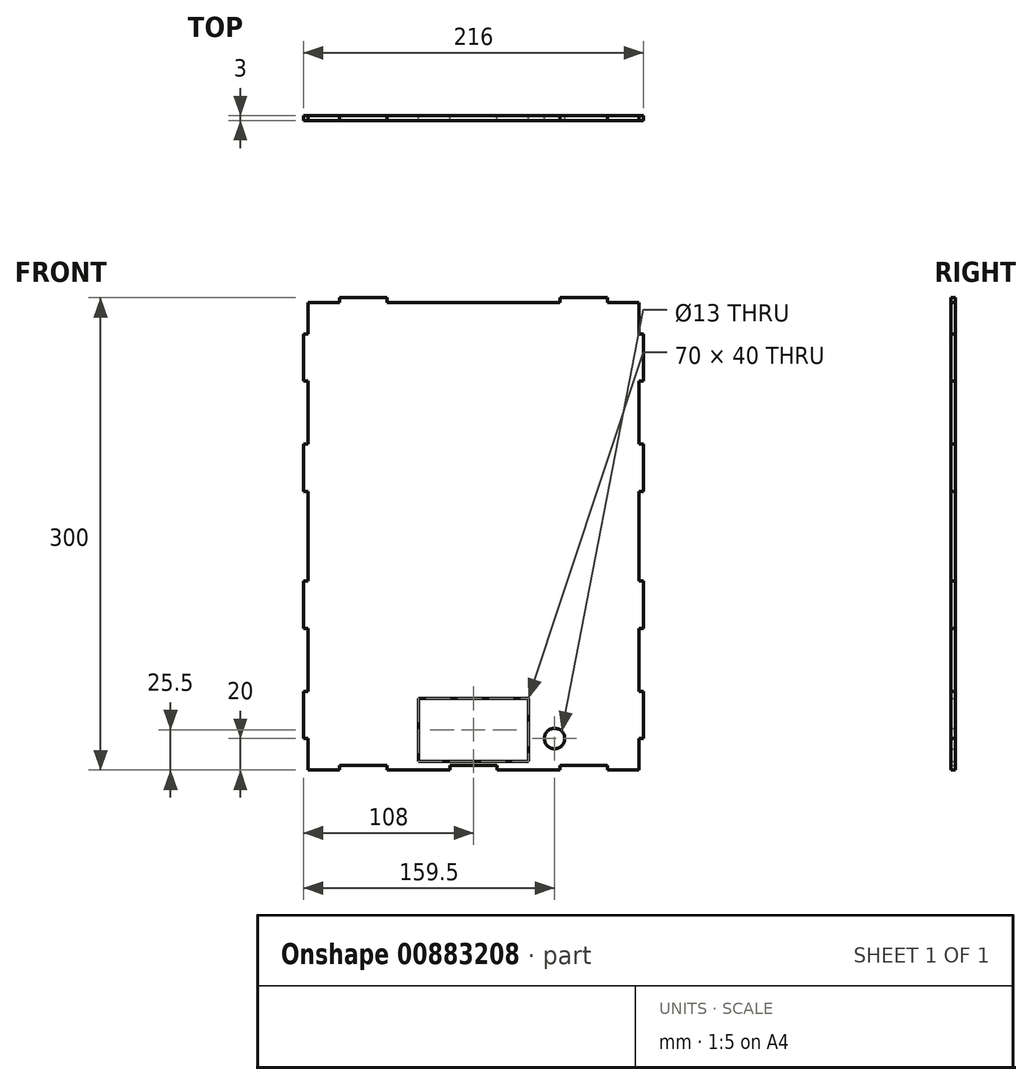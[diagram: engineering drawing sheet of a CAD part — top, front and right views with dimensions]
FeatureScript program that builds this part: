
annotation { "Feature Type Name" : "Feature", "Feature Type Description" : "" }
export const myFeature = defineFeature(function(context is Context, id is Id, definition is map)
    precondition{}
    {
        {
            var Q0;
            Q0=qCreatedBy(makeId("Front.planeOp"),FACE);
            var sketch = newSketch(context, id + "F0", { "sketchPlane" : qUnion([Q0])});
            skLineSegment(sketch, "E0.bottom", {"start": v(0, 0) * mm, "end": v(210, 0) * mm});
            skLineSegment(sketch, "E0.top", {"start": v(0, 297) * mm, "end": v(210, 297) * mm});
            skLineSegment(sketch, "E0.left", {"start": v(0, 0) * mm, "end": v(0, 297) * mm});
            skLineSegment(sketch, "E0.right", {"start": v(210, 0) * mm, "end": v(210, 297) * mm});
            skLineSegment(sketch, "E1", {"start": v(0, 277) * mm, "end": v(-3, 277) * mm});
            skLineSegment(sketch, "E2", {"start": v(-3, 277) * mm, "end": v(-3, 247) * mm});
            skLineSegment(sketch, "E3", {"start": v(-3, 247) * mm, "end": v(0, 247) * mm});
            skLineSegment(sketch, "E4.0.1.0", {"start": v(0, 207) * mm, "end": v(-3, 207) * mm});
            skLineSegment(sketch, "E4.0.1.1", {"start": v(-3, 207) * mm, "end": v(-3, 177) * mm});
            skLineSegment(sketch, "E4.0.1.2", {"start": v(-3, 177) * mm, "end": v(0, 177) * mm});
            skLineSegment(sketch, "E4.0.2.0", {"start": v(0, 120) * mm, "end": v(-3, 120) * mm});
            skLineSegment(sketch, "E4.0.2.1", {"start": v(-3, 120) * mm, "end": v(-3, 90) * mm});
            skLineSegment(sketch, "E4.0.2.2", {"start": v(-3, 90) * mm, "end": v(0, 90) * mm});
            skLineSegment(sketch, "E4.0.3.0", {"start": v(0, 50) * mm, "end": v(-3, 50) * mm});
            skLineSegment(sketch, "E4.0.3.1", {"start": v(-3, 50) * mm, "end": v(-3, 20) * mm});
            skLineSegment(sketch, "E4.0.3.2", {"start": v(-3, 20) * mm, "end": v(0, 20) * mm});
            skLineSegment(sketch, "E5", {"start": v(105, 297) * mm, "end": v(105, 0) * mm, "construction": true});
            skLineSegment(sketch, "E6.MirrorCS", {"start": v(210, 277) * mm, "end": v(213, 277) * mm});
            skLineSegment(sketch, "E7.MirrorCS", {"start": v(213, 277) * mm, "end": v(213, 247) * mm});
            skLineSegment(sketch, "E8.MirrorCS", {"start": v(213, 247) * mm, "end": v(210, 247) * mm});
            skLineSegment(sketch, "E9.MirrorCS", {"start": v(210, 207) * mm, "end": v(213, 207) * mm});
            skLineSegment(sketch, "E10.MirrorCS", {"start": v(213, 207) * mm, "end": v(213, 177) * mm});
            skLineSegment(sketch, "E11.MirrorCS", {"start": v(213, 177) * mm, "end": v(210, 177) * mm});
            skLineSegment(sketch, "E12.MirrorCS", {"start": v(210, 120) * mm, "end": v(213, 120) * mm});
            skLineSegment(sketch, "E13.MirrorCS", {"start": v(213, 120) * mm, "end": v(213, 90) * mm});
            skLineSegment(sketch, "E14.MirrorCS", {"start": v(213, 90) * mm, "end": v(210, 90) * mm});
            skLineSegment(sketch, "E15.MirrorCS", {"start": v(210, 50) * mm, "end": v(213, 50) * mm});
            skLineSegment(sketch, "E16.MirrorCS", {"start": v(213, 50) * mm, "end": v(213, 20) * mm});
            skLineSegment(sketch, "E17.MirrorCS", {"start": v(213, 20) * mm, "end": v(210, 20) * mm});
            skLineSegment(sketch, "E18", {"start": v(20, 0) * mm, "end": v(20, 3) * mm});
            skLineSegment(sketch, "E19", {"start": v(20, 3) * mm, "end": v(50, 3) * mm});
            skLineSegment(sketch, "E20", {"start": v(50, 3) * mm, "end": v(50, 0) * mm});
            skLineSegment(sketch, "E21", {"start": v(90, 0) * mm, "end": v(90, 3) * mm});
            skLineSegment(sketch, "E22", {"start": v(90, 3) * mm, "end": v(120, 3) * mm});
            skLineSegment(sketch, "E23", {"start": v(120, 3) * mm, "end": v(120, 0) * mm});
            skLineSegment(sketch, "E24", {"start": v(160, 0) * mm, "end": v(160, 3) * mm});
            skLineSegment(sketch, "E25", {"start": v(160, 3) * mm, "end": v(190, 3) * mm});
            skLineSegment(sketch, "E26", {"start": v(190, 3) * mm, "end": v(190, 0) * mm});
            skPoint(sketch, "E27", {"position": v(105, 3) * mm});
            skLineSegment(sketch, "E28.bottom", {"start": v(70, 45.5) * mm, "end": v(140, 45.5) * mm});
            skLineSegment(sketch, "E28.left", {"start": v(70, 45.5) * mm, "end": v(70, 5.5) * mm});
            skLineSegment(sketch, "E28.right", {"start": v(140, 45.5) * mm, "end": v(140, 5.5) * mm});
            skPoint(sketch, "E29", {"position": v(105, 45.5) * mm});
            skLineSegment(sketch, "E30", {"start": v(190, 297) * mm, "end": v(190, 300) * mm});
            skLineSegment(sketch, "E31", {"start": v(190, 300) * mm, "end": v(160, 300) * mm});
            skLineSegment(sketch, "E32", {"start": v(160, 300) * mm, "end": v(160, 297) * mm});
            skLineSegment(sketch, "E33", {"start": v(50, 297) * mm, "end": v(50, 300) * mm});
            skLineSegment(sketch, "E34", {"start": v(50, 300) * mm, "end": v(20, 300) * mm});
            skLineSegment(sketch, "E35", {"start": v(20, 300) * mm, "end": v(20, 297) * mm});
            skLineSegment(sketch, "E36", {"start": v(140, 5.5) * mm, "end": v(70, 5.5) * mm});
            skCircle(sketch, "E37", {"center": v(156.5, 20) * mm, "radius": 6.5 * mm});
            skSolve(sketch);
        }
        {
            var Q0;
            {var subQ0=sQuery(id+"F0.wireOp",EDGE,"E4.0.3.0");Q0=makeQuery(id+"F0.imprint","IMPRINT",FACE,{"disambiguationData":[TD([[makeQuery(id+"F0.imprint","IMPRINT",EDGE,{"derivedFrom":subQ0}),1.0]])]});}
            var Q1;
            {var subQ0=sQuery(id+"F0.wireOp",EDGE,"E4.0.2.0");Q1=makeQuery(id+"F0.imprint","IMPRINT",FACE,{"disambiguationData":[TD([[makeQuery(id+"F0.imprint","IMPRINT",EDGE,{"derivedFrom":subQ0}),1.0]])]});}
            var Q2;
            {var subQ0=sQuery(id+"F0.wireOp",EDGE,"E4.0.1.0");Q2=makeQuery(id+"F0.imprint","IMPRINT",FACE,{"disambiguationData":[TD([[makeQuery(id+"F0.imprint","IMPRINT",EDGE,{"derivedFrom":subQ0}),1.0]])]});}
            var Q3;
            {var subQ0=sQuery(id+"F0.wireOp",EDGE,"E1");Q3=makeQuery(id+"F0.imprint","IMPRINT",FACE,{"disambiguationData":[TD([[makeQuery(id+"F0.imprint","IMPRINT",EDGE,{"derivedFrom":subQ0}),1.0]])]});}
            var Q4;
            {var subQ0=sQuery(id+"F0.wireOp",EDGE,"E15.MirrorCS");Q4=makeQuery(id+"F0.imprint","IMPRINT",FACE,{"disambiguationData":[TD([[makeQuery(id+"F0.imprint","IMPRINT",EDGE,{"derivedFrom":subQ0}),-1.0]])]});}
            var Q5;
            {var subQ0=sQuery(id+"F0.wireOp",EDGE,"E12.MirrorCS");Q5=makeQuery(id+"F0.imprint","IMPRINT",FACE,{"disambiguationData":[TD([[makeQuery(id+"F0.imprint","IMPRINT",EDGE,{"derivedFrom":subQ0}),-1.0]])]});}
            var Q6;
            {var subQ0=sQuery(id+"F0.wireOp",EDGE,"E9.MirrorCS");Q6=makeQuery(id+"F0.imprint","IMPRINT",FACE,{"disambiguationData":[TD([[makeQuery(id+"F0.imprint","IMPRINT",EDGE,{"derivedFrom":subQ0}),-1.0]])]});}
            var Q7;
            {var subQ0=sQuery(id+"F0.wireOp",EDGE,"E6.MirrorCS");Q7=makeQuery(id+"F0.imprint","IMPRINT",FACE,{"disambiguationData":[TD([[makeQuery(id+"F0.imprint","IMPRINT",EDGE,{"derivedFrom":subQ0}),-1.0]])]});}
            var Q8;
            {var subQ12=sQuery(id+"F0.wireOp",EDGE,"E0.top");Q8=makeQuery(id+"F0.imprint","IMPRINT",FACE,{"disambiguationData":[TD([[makeQuery(id+"F0.imprint","IMPRINT",EDGE,{"derivedFrom":subQ12}),-1.0]])]});}
            var Q9;
            {var subQ0=sQuery(id+"F0.wireOp",EDGE,"E30");Q9=makeQuery(id+"F0.imprint","IMPRINT",FACE,{"disambiguationData":[TD([[makeQuery(id+"F0.imprint","IMPRINT",EDGE,{"derivedFrom":subQ0}),1.0]])]});}
            var Q10;
            {var subQ0=sQuery(id+"F0.wireOp",EDGE,"E33");Q10=makeQuery(id+"F0.imprint","IMPRINT",FACE,{"disambiguationData":[TD([[makeQuery(id+"F0.imprint","IMPRINT",EDGE,{"derivedFrom":subQ0}),1.0]])]});}
            extrude(context, id + "F1", {"entities" : qUnion([Q0, Q1, Q2, Q3, Q4, Q5, Q6, Q7, Q8, Q9, Q10]), "depth" : 3 * mm, "offsetDistance" : 25 * mm});
        }
    });
